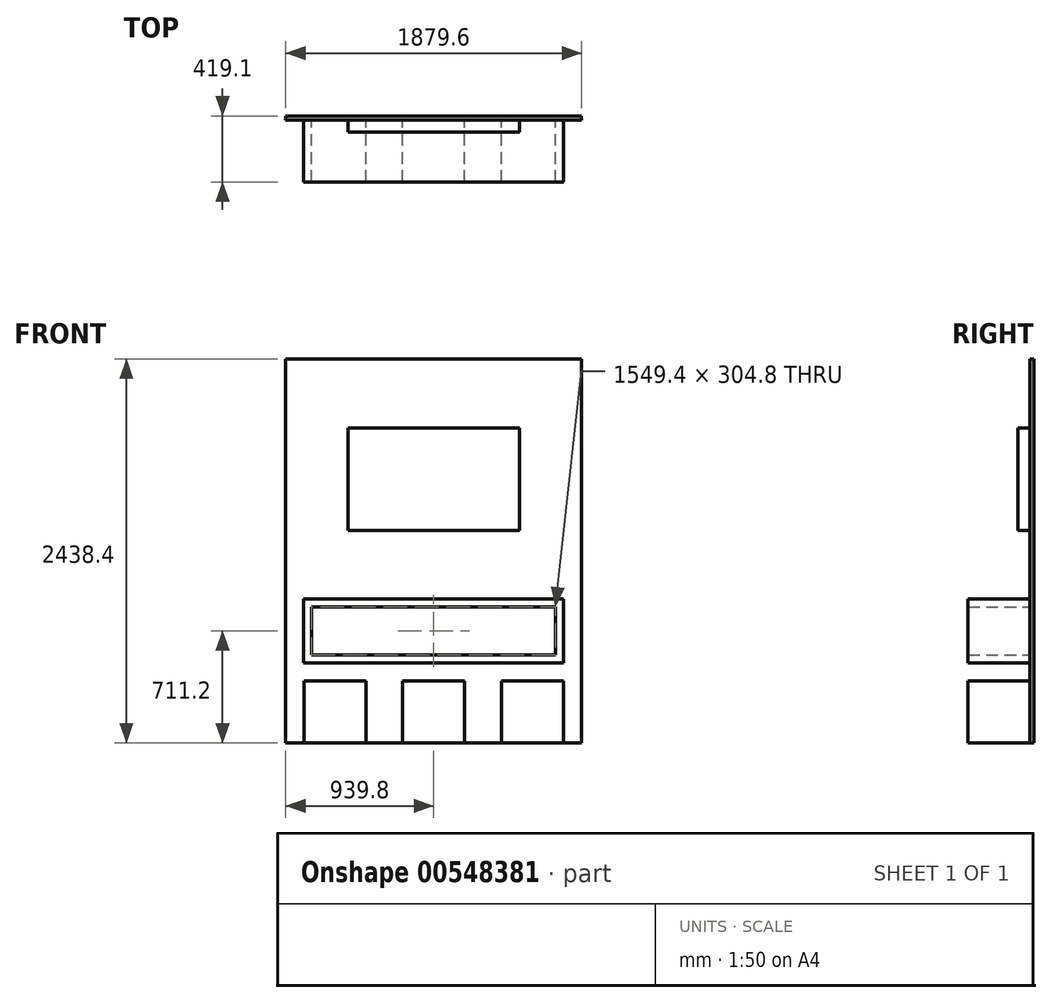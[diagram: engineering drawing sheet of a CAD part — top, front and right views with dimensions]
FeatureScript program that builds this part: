
annotation { "Feature Type Name" : "Feature", "Feature Type Description" : "" }
export const myFeature = defineFeature(function(context is Context, id is Id, definition is map)
    precondition{}
    {
        {
            var Q0;
            Q0=qCreatedBy(makeId("Front.planeOp"),FACE);
            var sketch = newSketch(context, id + "F0", { "sketchPlane" : qUnion([Q0])});
            skLineSegment(sketch, "E0.bottom", {"start": v(939.8, -1219.2) * mm, "end": v(-939.8, -1219.2) * mm});
            skLineSegment(sketch, "E0.top", {"start": v(939.8, 1219.2) * mm, "end": v(-939.8, 1219.2) * mm});
            skLineSegment(sketch, "E0.left", {"start": v(939.8, -1219.2) * mm, "end": v(939.8, 1219.2) * mm});
            skLineSegment(sketch, "E0.right", {"start": v(-939.8, -1219.2) * mm, "end": v(-939.8, 1219.2) * mm});
            skPoint(sketch, "E0.middle", {"position": v(0, 0) * mm});
            skSolve(sketch);
        }
        {
            var Q0;
            Q0 = qSketchRegion(id + "F0", true);
            extrude(context, id + "F1", {"entities" : qUnion([Q0]), "depth" : 25.4 * mm, "offsetDistance" : 25.4 * mm});
        }
        {
            var Q0;
            Q0=makeQuery(id+"F1.opExtrude","CAP_FACE",FACE,{"disambiguationData":[OSD([sQuery(id+"F0.wireOp",EDGE,"E0.bottom"),sQuery(id+"F0.wireOp",EDGE,"E0.top"),sQuery(id+"F0.wireOp",EDGE,"E0.left"),sQuery(id+"F0.wireOp",EDGE,"E0.right")])],"isStart":false});
            var sketch = newSketch(context, id + "F2", { "sketchPlane" : qUnion([Q0])});
            skLineSegment(sketch, "E1", {"start": v(0, 1219.2) * mm, "end": v(0, 457.2) * mm, "construction": true});
            skLineSegment(sketch, "E2.bottom", {"start": v(-545.14, 782.84) * mm, "end": v(545.14, 782.84) * mm});
            skLineSegment(sketch, "E2.top", {"start": v(-545.14, 131.56) * mm, "end": v(545.14, 131.56) * mm});
            skLineSegment(sketch, "E2.left", {"start": v(-545.14, 782.84) * mm, "end": v(-545.14, 131.56) * mm});
            skLineSegment(sketch, "E2.right", {"start": v(545.14, 782.84) * mm, "end": v(545.14, 131.56) * mm});
            skPoint(sketch, "E2.middle", {"position": v(0, 457.2) * mm});
            skLineSegment(sketch, "E3", {"start": v(-939.8, -1219.2) * mm, "end": v(-313.27, -1219.2) * mm, "construction": true});
            skLineSegment(sketch, "E4", {"start": v(-313.27, -1219.2) * mm, "end": v(313.27, -1219.2) * mm, "construction": true});
            skLineSegment(sketch, "E5", {"start": v(313.27, -1219.2) * mm, "end": v(939.8, -1219.2) * mm, "construction": true});
            skLineSegment(sketch, "E6.bottom", {"start": v(-823.38, -1219.2) * mm, "end": v(-429.68, -1219.2) * mm});
            skLineSegment(sketch, "E6.top", {"start": v(-823.38, -825.5) * mm, "end": v(-429.68, -825.5) * mm});
            skLineSegment(sketch, "E6.left", {"start": v(-823.38, -1219.2) * mm, "end": v(-823.38, -825.5) * mm});
            skLineSegment(sketch, "E6.right", {"start": v(-429.68, -1219.2) * mm, "end": v(-429.68, -825.5) * mm});
            skLineSegment(sketch, "E7.bottom", {"start": v(429.68, -1219.2) * mm, "end": v(823.38, -1219.2) * mm});
            skLineSegment(sketch, "E7.top", {"start": v(429.68, -825.5) * mm, "end": v(823.38, -825.5) * mm});
            skLineSegment(sketch, "E7.left", {"start": v(429.68, -1219.2) * mm, "end": v(429.68, -825.5) * mm});
            skLineSegment(sketch, "E7.right", {"start": v(823.38, -1219.2) * mm, "end": v(823.38, -825.5) * mm});
            skLineSegment(sketch, "E8", {"start": v(-939.8, -1219.2) * mm, "end": v(-626.53, -1219.2) * mm, "construction": true});
            skLineSegment(sketch, "E9", {"start": v(-313.27, -1219.2) * mm, "end": v(0, -1219.2) * mm, "construction": true});
            skLineSegment(sketch, "E10", {"start": v(313.27, -1219.2) * mm, "end": v(626.53, -1219.2) * mm, "construction": true});
            skLineSegment(sketch, "E11.bottom", {"start": v(-196.85, -1219.2) * mm, "end": v(196.85, -1219.2) * mm});
            skLineSegment(sketch, "E11.top", {"start": v(-196.85, -825.5) * mm, "end": v(196.85, -825.5) * mm});
            skLineSegment(sketch, "E11.left", {"start": v(-196.85, -1219.2) * mm, "end": v(-196.85, -825.5) * mm});
            skLineSegment(sketch, "E11.right", {"start": v(196.85, -1219.2) * mm, "end": v(196.85, -825.5) * mm});
            skLineSegment(sketch, "E12", {"start": v(0, -1219.2) * mm, "end": v(0, -711.2) * mm, "construction": true});
            skLineSegment(sketch, "E13.bottom", {"start": v(-825.5, -711.2) * mm, "end": v(825.5, -711.2) * mm});
            skLineSegment(sketch, "E13.top", {"start": v(-825.5, -304.8) * mm, "end": v(825.5, -304.8) * mm});
            skLineSegment(sketch, "E13.left", {"start": v(825.5, -711.2) * mm, "end": v(825.5, -304.8) * mm});
            skLineSegment(sketch, "E13.right", {"start": v(-825.5, -711.2) * mm, "end": v(-825.5, -304.8) * mm});
            skLineSegment(sketch, "E14.0", {"start": v(-774.7, -355.6) * mm, "end": v(774.7, -355.6) * mm});
            skLineSegment(sketch, "E14.1", {"start": v(-774.7, -660.4) * mm, "end": v(-774.7, -355.6) * mm});
            skLineSegment(sketch, "E14.2", {"start": v(-774.7, -660.4) * mm, "end": v(774.7, -660.4) * mm});
            skLineSegment(sketch, "E14.3", {"start": v(774.7, -660.4) * mm, "end": v(774.7, -355.6) * mm});
            skLineSegment(sketch, "E15.0", {"start": v(946.15, -1225.55) * mm, "end": v(946.15, 1225.55) * mm});
            skLineSegment(sketch, "E15.1", {"start": v(-946.15, -1225.55) * mm, "end": v(946.15, -1225.55) * mm});
            skLineSegment(sketch, "E15.2", {"start": v(-946.15, 1225.55) * mm, "end": v(-946.15, -1225.55) * mm});
            skLineSegment(sketch, "E15.3", {"start": v(946.15, 1225.55) * mm, "end": v(-946.15, 1225.55) * mm});
            skSolve(sketch);
        }
        {
            var Q0;
            Q0=makeQuery(id+"F2.imprint","IMPRINT",FACE,{"disambiguationData":[TD([[makeQuery(id+"F2.imprint","IMPRINT",EDGE,{"derivedFrom":sQuery(id+"F2.wireOp",EDGE,"E2.bottom")}),-1.0]])]});
            extrude(context, id + "F3", {"entities" : qUnion([Q0]), "depth" : 76.2 * mm, "offsetDistance" : 25.4 * mm});
        }
        {
            var Q0;
            Q0=makeQuery(id+"F2.imprint","IMPRINT",FACE,{"disambiguationData":[TD([[makeQuery(id+"F2.imprint","IMPRINT",EDGE,{"derivedFrom":sQuery(id+"F2.wireOp",EDGE,"E6.bottom")}),-1.0]])]});
            var Q1;
            Q1=makeQuery(id+"F2.imprint","IMPRINT",FACE,{"disambiguationData":[TD([[makeQuery(id+"F2.imprint","IMPRINT",EDGE,{"derivedFrom":sQuery(id+"F2.wireOp",EDGE,"E11.bottom")}),-1.0]])]});
            var Q2;
            Q2=makeQuery(id+"F2.imprint","IMPRINT",FACE,{"disambiguationData":[TD([[makeQuery(id+"F2.imprint","IMPRINT",EDGE,{"derivedFrom":sQuery(id+"F2.wireOp",EDGE,"E7.bottom")}),-1.0]])]});
            extrude(context, id + "F4", {"entities" : qUnion([Q0, Q1, Q2]), "depth" : 393.7 * mm, "offsetDistance" : 25.4 * mm});
        }
        {
            var Q0;
            Q0=makeQuery(id+"F2.imprint","IMPRINT",FACE,{"disambiguationData":[TD([[makeQuery(id+"F2.imprint","IMPRINT",EDGE,{"derivedFrom":sQuery(id+"F2.wireOp",EDGE,"E13.bottom")}),1.0]])]});
            extrude(context, id + "F5", {"entities" : qUnion([Q0]), "depth" : 393.7 * mm, "offsetDistance" : 25.4 * mm});
        }
    });
